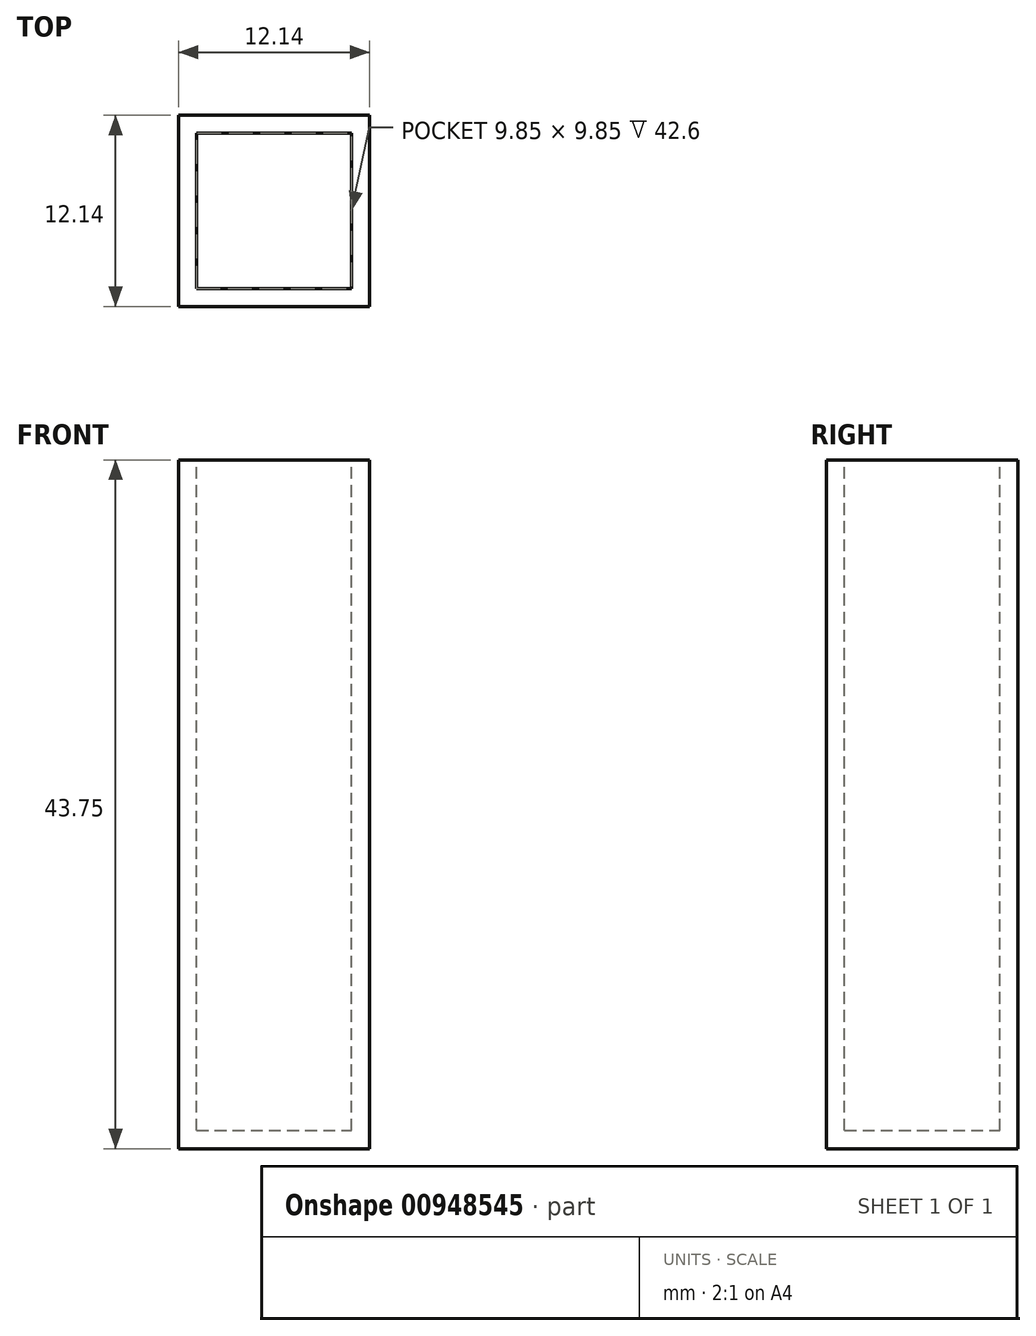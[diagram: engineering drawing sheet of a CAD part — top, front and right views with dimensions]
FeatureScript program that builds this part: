
annotation { "Feature Type Name" : "Feature", "Feature Type Description" : "" }
export const myFeature = defineFeature(function(context is Context, id is Id, definition is map)
    precondition{}
    {
        {
            var Q0;
            Q0=qCreatedBy(makeId("Top.planeOp"),FACE);
            var sketch = newSketch(context, id + "F0", { "sketchPlane" : qUnion([Q0])});
            skLineSegment(sketch, "E0.bottom", {"start": v(6.08, 6.07) * mm, "end": v(-6.07, 6.07) * mm});
            skLineSegment(sketch, "E0.top", {"start": v(6.08, -6.08) * mm, "end": v(-6.08, -6.08) * mm});
            skLineSegment(sketch, "E0.left", {"start": v(6.08, 6.07) * mm, "end": v(6.08, -6.08) * mm});
            skLineSegment(sketch, "E0.right", {"start": v(-6.08, 6.08) * mm, "end": v(-6.08, -6.08) * mm});
            skPoint(sketch, "E0.middle", {"position": v(0, 0) * mm});
            skSolve(sketch);
        }
        {
            var Q0;
            Q0=makeQuery(id+"F0.imprint","IMPRINT",FACE,{"disambiguationData":[TD([[makeQuery(id+"F0.imprint","IMPRINT",EDGE,{"derivedFrom":sQuery(id+"F0.wireOp",EDGE,"E0.bottom")}),1.0]])]});
            extrude(context, id + "F1", {"entities" : qUnion([Q0]), "depth" : 43.75 * mm, "offsetDistance" : 25 * mm});
        }
        {
            var Q0;
            Q0=makeQuery(id+"F1.opExtrude","CAP_FACE",FACE,{"disambiguationData":[OSD([sQuery(id+"F0.wireOp",EDGE,"E0.bottom"),sQuery(id+"F0.wireOp",EDGE,"E0.top"),sQuery(id+"F0.wireOp",EDGE,"E0.left"),sQuery(id+"F0.wireOp",EDGE,"E0.right")])],"isStart":false});
            var sketch = newSketch(context, id + "F2", { "sketchPlane" : qUnion([Q0])});
            skLineSegment(sketch, "E1.bottom", {"start": v(4.93, 4.93) * mm, "end": v(-4.93, 4.93) * mm});
            skLineSegment(sketch, "E1.top", {"start": v(4.93, -4.93) * mm, "end": v(-4.93, -4.93) * mm});
            skLineSegment(sketch, "E1.left", {"start": v(4.93, 4.93) * mm, "end": v(4.93, -4.93) * mm});
            skLineSegment(sketch, "E1.right", {"start": v(-4.93, 4.93) * mm, "end": v(-4.93, -4.93) * mm});
            skPoint(sketch, "E1.middle", {"position": v(0, 0) * mm});
            skSolve(sketch);
        }
        {
            var Q0;
            Q0=makeQuery(id+"F2.imprint","IMPRINT",FACE,{"disambiguationData":[TD([[makeQuery(id+"F2.imprint","IMPRINT",EDGE,{"derivedFrom":sQuery(id+"F2.wireOp",EDGE,"E1.bottom")}),1.0]])]});
            var Q1;
            Q1=makeQuery(id+"F1.opExtrude","CAP_FACE",FACE,{"disambiguationData":[OSD([sQuery(id+"F0.wireOp",EDGE,"E0.bottom"),sQuery(id+"F0.wireOp",EDGE,"E0.top"),sQuery(id+"F0.wireOp",EDGE,"E0.left"),sQuery(id+"F0.wireOp",EDGE,"E0.right")])],"isStart":true});
            extrude(context, id + "F3", {"entities" : qUnion([Q0]), "operationType" : NewBodyOperationType.REMOVE, "endBound" : BoundingType.UP_TO_SURFACE, "oppositeDirection" : true, "depth" : 25 * mm, "endBoundEntityFace" : qUnion([Q1]), "hasOffset" : true, "offsetDistance" : 1.15 * mm});
        }
    });
